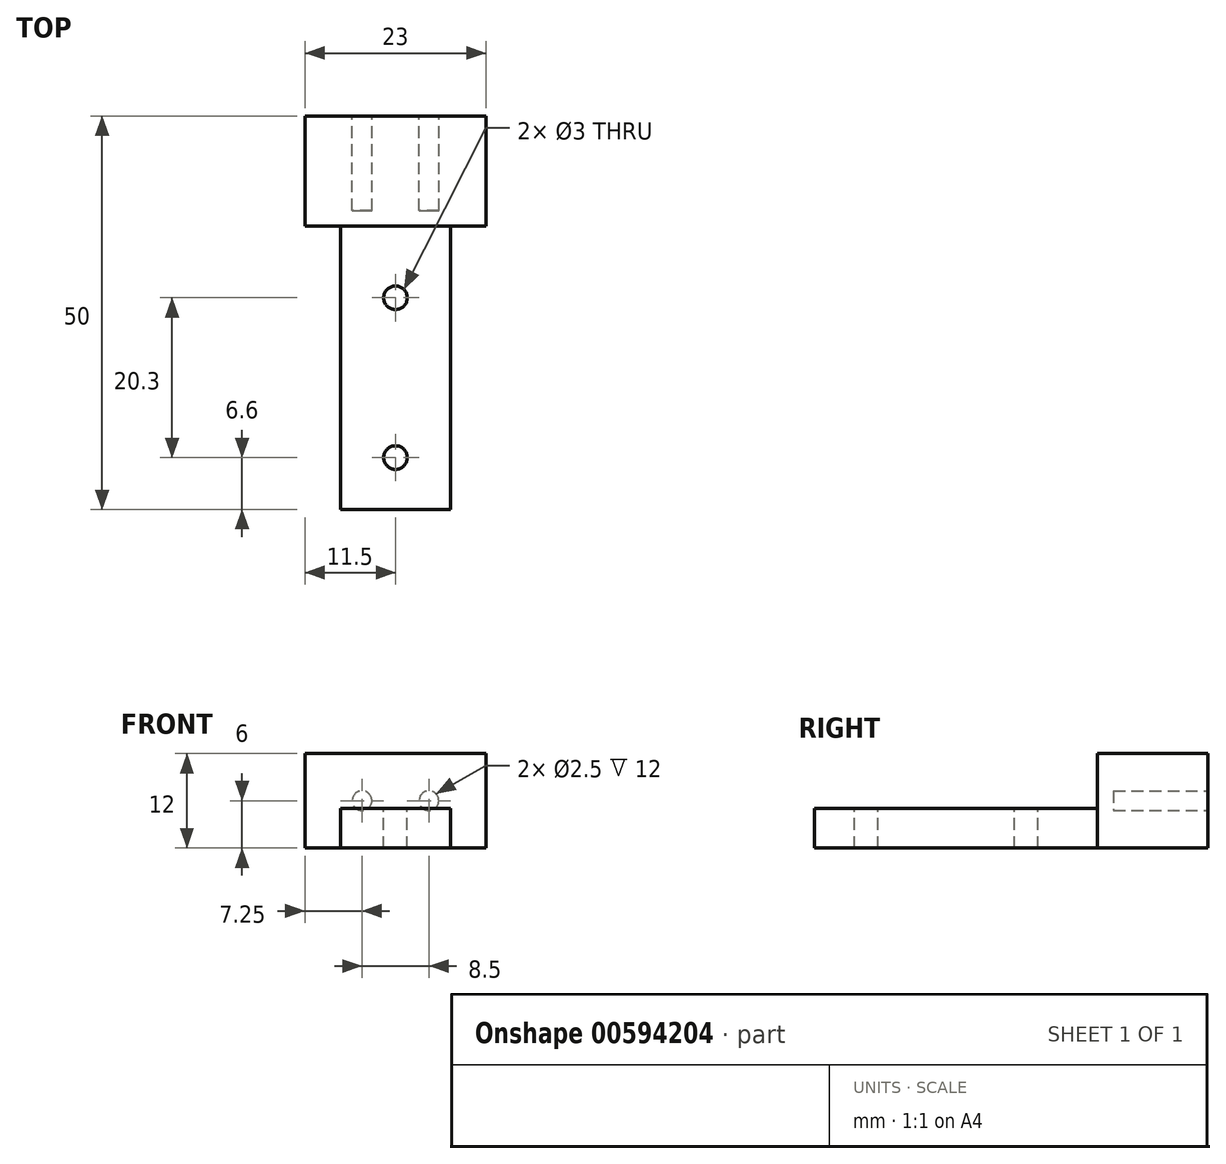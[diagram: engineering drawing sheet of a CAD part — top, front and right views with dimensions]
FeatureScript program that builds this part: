
annotation { "Feature Type Name" : "Feature", "Feature Type Description" : "" }
export const myFeature = defineFeature(function(context is Context, id is Id, definition is map)
    precondition{}
    {
        {
            var Q0;
            Q0=qCreatedBy(makeId("Top.planeOp"),FACE);
            var sketch = newSketch(context, id + "F0", { "sketchPlane" : qUnion([Q0])});
            skLineSegment(sketch, "E0.bottom", {"start": v(0, 0) * mm, "end": v(14, 0) * mm});
            skLineSegment(sketch, "E0.top", {"start": v(0, 58) * mm, "end": v(14, 58) * mm});
            skLineSegment(sketch, "E0.left", {"start": v(0, 0) * mm, "end": v(0, 58) * mm});
            skLineSegment(sketch, "E0.right", {"start": v(14, 0) * mm, "end": v(14, 58) * mm});
            skSolve(sketch);
        }
        {
            var Q0;
            Q0=makeQuery(id+"F0.imprint","IMPRINT",FACE,{"disambiguationData":[TD([[makeQuery(id+"F0.imprint","IMPRINT",EDGE,{"derivedFrom":sQuery(id+"F0.wireOp",EDGE,"E0.bottom")}),1.0]])]});
            extrude(context, id + "F1", {"entities" : qUnion([Q0]), "depth" : 5 * mm, "offsetDistance" : 25 * mm});
        }
        {
            var Q0;
            Q0=makeQuery(id+"F1.opExtrude","CAP_FACE",FACE,{"disambiguationData":[OSD([sQuery(id+"F0.wireOp",EDGE,"E0.bottom"),sQuery(id+"F0.wireOp",EDGE,"E0.top"),sQuery(id+"F0.wireOp",EDGE,"E0.left"),sQuery(id+"F0.wireOp",EDGE,"E0.right")])],"isStart":false});
            var sketch = newSketch(context, id + "F2", { "sketchPlane" : qUnion([Q0])});
            skLineSegment(sketch, "E1.bottom", {"start": v(0, 58) * mm, "end": v(14, 58) * mm});
            skLineSegment(sketch, "E1.top", {"start": v(0, 49.67) * mm, "end": v(14, 49.67) * mm});
            skLineSegment(sketch, "E1.left", {"start": v(0, 58) * mm, "end": v(0, 49.67) * mm});
            skLineSegment(sketch, "E1.right", {"start": v(14, 58) * mm, "end": v(14, 49.67) * mm});
            skLineSegment(sketch, "E2.bottom", {"start": v(0, 58) * mm, "end": v(1.75, 58) * mm});
            skLineSegment(sketch, "E2.top", {"start": v(0, 55.5) * mm, "end": v(1.75, 55.5) * mm});
            skLineSegment(sketch, "E2.left", {"start": v(0, 58) * mm, "end": v(0, 55.5) * mm});
            skLineSegment(sketch, "E2.right", {"start": v(1.75, 58) * mm, "end": v(1.75, 55.5) * mm});
            skLineSegment(sketch, "E3.bottom", {"start": v(14, 58) * mm, "end": v(12.25, 58) * mm});
            skLineSegment(sketch, "E3.top", {"start": v(14, 55.5) * mm, "end": v(12.25, 55.5) * mm});
            skLineSegment(sketch, "E3.left", {"start": v(14, 58) * mm, "end": v(14, 55.5) * mm});
            skLineSegment(sketch, "E3.right", {"start": v(12.25, 58) * mm, "end": v(12.25, 55.5) * mm});
            skCircle(sketch, "E4", {"center": v(1.75, 55.5) * mm, "radius": 1 * mm});
            skCircle(sketch, "E5", {"center": v(12.25, 55.5) * mm, "radius": 1 * mm});
            skLineSegment(sketch, "E6.bottom", {"start": v(1.75, 55.5) * mm, "end": v(7, 55.5) * mm});
            skLineSegment(sketch, "E6.top", {"start": v(1.75, 36.5) * mm, "end": v(7, 36.5) * mm});
            skLineSegment(sketch, "E6.left", {"start": v(1.75, 55.5) * mm, "end": v(1.75, 36.5) * mm});
            skLineSegment(sketch, "E6.right", {"start": v(7, 55.5) * mm, "end": v(7, 36.5) * mm});
            skLineSegment(sketch, "E7.top", {"start": v(1.75, 28.4) * mm, "end": v(7, 28.4) * mm});
            skLineSegment(sketch, "E7.left", {"start": v(1.75, 36.5) * mm, "end": v(1.75, 28.4) * mm});
            skLineSegment(sketch, "E7.right", {"start": v(7, 36.5) * mm, "end": v(7, 28.4) * mm});
            skLineSegment(sketch, "E8.top", {"start": v(1.75, 26.9) * mm, "end": v(7, 26.9) * mm});
            skLineSegment(sketch, "E8.left", {"start": v(1.75, 28.4) * mm, "end": v(1.75, 26.9) * mm});
            skLineSegment(sketch, "E8.right", {"start": v(7, 28.4) * mm, "end": v(7, 26.9) * mm});
            skCircle(sketch, "E9", {"center": v(7, 26.9) * mm, "radius": 1.5 * mm});
            skLineSegment(sketch, "E10.bottom", {"start": v(7, 26.9) * mm, "end": v(12.25, 26.9) * mm});
            skLineSegment(sketch, "E10.top", {"start": v(7, 6.6) * mm, "end": v(12.25, 6.6) * mm});
            skLineSegment(sketch, "E10.left", {"start": v(7, 26.9) * mm, "end": v(7, 6.6) * mm});
            skLineSegment(sketch, "E10.right", {"start": v(12.25, 26.9) * mm, "end": v(12.25, 6.6) * mm});
            skCircle(sketch, "E11", {"center": v(7, 6.6) * mm, "radius": 1.5 * mm});
            skSolve(sketch);
        }
        {
            var Q0;
            {var subQ0=sQuery(id+"F2.wireOp",EDGE,"E8.right");Q0=makeQuery(id+"F2.imprint","IMPRINT",FACE,{"disambiguationData":[TD([[makeQuery(id+"F2.imprint","IMPRINT",EDGE,{"derivedFrom":subQ0}),1.0]])]});}
            var Q1;
            {var subQ0=sQuery(id+"F2.wireOp",EDGE,"E8.right");Q1=makeQuery(id+"F2.imprint","IMPRINT",FACE,{"disambiguationData":[TD([[makeQuery(id+"F2.imprint","IMPRINT",EDGE,{"derivedFrom":subQ0}),-1.0]])]});}
            var Q2;
            {var subQ1=sQuery(id+"F2.wireOp",EDGE,"E8.top");var subQ3=sQuery(id+"F2.wireOp",EDGE,"E9");var subQ4=makeQuery(id+"F2.imprint","INTERSECT",VERTEX,{"derivedFrom":[subQ1,subQ3]});Q2=makeQuery(id+"F2.imprint","IMPRINT",FACE,{"disambiguationData":[TD([[makeQuery(id+"F2.imprint","IMPRINT",EDGE,{"disambiguationData":[TD([[subQ4,-1.0]])],"derivedFrom":subQ3}),1.0]])]});}
            var Q3;
            {var subQ0=sQuery(id+"F2.wireOp",EDGE,"E10.bottom");var subQ1=sQuery(id+"F2.wireOp",EDGE,"E9");var subQ2=makeQuery(id+"F2.imprint","INTERSECT",VERTEX,{"derivedFrom":[subQ1,subQ0]});Q3=makeQuery(id+"F2.imprint","IMPRINT",FACE,{"disambiguationData":[TD([[makeQuery(id+"F2.imprint","IMPRINT",EDGE,{"disambiguationData":[TD([[subQ2,1.0]])],"derivedFrom":subQ1}),1.0]])]});}
            var Q4;
            {var subQ0=sQuery(id+"F2.wireOp",EDGE,"E10.left");var subQ1=sQuery(id+"F2.wireOp",EDGE,"E10.top");var subQ2=makeQuery(id+"F2.imprint","INTERSECT",VERTEX,{"derivedFrom":[subQ1,subQ0]});Q4=makeQuery(id+"F2.imprint","IMPRINT",FACE,{"disambiguationData":[TD([[makeQuery(id+"F2.imprint","IMPRINT",EDGE,{"disambiguationData":[TD([[subQ2,-1.0]])],"derivedFrom":subQ1}),1.0]])]});}
            var Q5;
            {var subQ0=sQuery(id+"F2.wireOp",EDGE,"E10.left");var subQ1=sQuery(id+"F2.wireOp",EDGE,"E10.top");var subQ2=makeQuery(id+"F2.imprint","INTERSECT",VERTEX,{"derivedFrom":[subQ1,subQ0]});Q5=makeQuery(id+"F2.imprint","IMPRINT",FACE,{"disambiguationData":[TD([[makeQuery(id+"F2.imprint","IMPRINT",EDGE,{"disambiguationData":[TD([[subQ2,-1.0]])],"derivedFrom":subQ1}),-1.0]])]});}
            extrude(context, id + "F3", {"entities" : qUnion([Q0, Q1, Q2, Q3, Q4, Q5]), "operationType" : NewBodyOperationType.REMOVE, "oppositeDirection" : true, "depth" : 25 * mm, "offsetDistance" : 25 * mm});
        }
        {
            var Q0;
            Q0=makeQuery(id+"F1.opExtrude","SWEPT_FACE",FACE,{"disambiguationData":[OSD([sQuery(id+"F0.wireOp",EDGE,"E0.top")])]});
            cPlane(context, id + "F4", {"entities" : qUnion([Q0]), "cplaneType" : CPlaneType.OFFSET, "offset" : 2.5 * mm, "oppositeDirection" : true, "width" : 150 * mm, "height" : 150 * mm});
        }
        {
            var Q0;
            Q0=qCreatedBy(id+"F4.planeOp",FACE);
            var sketch = newSketch(context, id + "F5", { "sketchPlane" : qUnion([Q0])});
            skLineSegment(sketch, "E12.bottom", {"start": v(0, 0) * mm, "end": v(4.5, 0) * mm});
            skLineSegment(sketch, "E12.top", {"start": v(0, -3.5) * mm, "end": v(4.5, -3.5) * mm});
            skLineSegment(sketch, "E12.left", {"start": v(0, 0) * mm, "end": v(0, -3.5) * mm});
            skLineSegment(sketch, "E12.right", {"start": v(4.5, 0) * mm, "end": v(4.5, -3.5) * mm});
            skLineSegment(sketch, "E13.bottom", {"start": v(4.5, -3.5) * mm, "end": v(-18.5, -3.5) * mm});
            skLineSegment(sketch, "E13.top", {"start": v(4.5, 8.5) * mm, "end": v(-18.5, 8.5) * mm});
            skLineSegment(sketch, "E13.left", {"start": v(4.5, -3.5) * mm, "end": v(4.5, 8.5) * mm});
            skLineSegment(sketch, "E13.right", {"start": v(-18.5, -3.5) * mm, "end": v(-18.5, 8.5) * mm});
            skLineSegment(sketch, "E14.bottom", {"start": v(4.5, 0) * mm, "end": v(-18.5, 0) * mm});
            skLineSegment(sketch, "E14.top", {"start": v(4.5, 12) * mm, "end": v(-18.5, 12) * mm});
            skLineSegment(sketch, "E14.left", {"start": v(4.5, 0) * mm, "end": v(4.5, 12) * mm});
            skLineSegment(sketch, "E14.right", {"start": v(-18.5, 0) * mm, "end": v(-18.5, 12) * mm});
            skSolve(sketch);
        }
        {
            var Q0;
            {var subQ0=sQuery(id+"F5.wireOp",EDGE,"E13.top");Q0=makeQuery(id+"F5.imprint","IMPRINT",FACE,{"disambiguationData":[TD([[makeQuery(id+"F5.imprint","IMPRINT",EDGE,{"derivedFrom":subQ0}),-1.0]])]});}
            var Q1;
            {var subQ1=sQuery(id+"F5.wireOp",EDGE,"E13.top");Q1=makeQuery(id+"F5.imprint","IMPRINT",FACE,{"disambiguationData":[TD([[makeQuery(id+"F5.imprint","IMPRINT",EDGE,{"derivedFrom":subQ1}),1.0]])]});}
            extrude(context, id + "F6", {"entities" : qUnion([Q0, Q1]), "operationType" : NewBodyOperationType.ADD, "oppositeDirection" : true, "depth" : 19.5 * mm, "offsetDistance" : 25 * mm});
        }
        {
            var Q0;
            Q0=makeQuery(id+"F1.opExtrude","SWEPT_FACE",FACE,{"disambiguationData":[OSD([sQuery(id+"F0.wireOp",EDGE,"E0.top")])]});
            var sketch = newSketch(context, id + "F7", { "sketchPlane" : qUnion([Q0])});
            skLineSegment(sketch, "E15.bottom", {"start": v(0, 0) * mm, "end": v(-18.5, 0) * mm});
            skLineSegment(sketch, "E15.top", {"start": v(0, 8.5) * mm, "end": v(-18.5, 8.5) * mm});
            skLineSegment(sketch, "E15.left", {"start": v(0, 0) * mm, "end": v(0, 8.5) * mm});
            skLineSegment(sketch, "E15.right", {"start": v(-18.5, 0) * mm, "end": v(-18.5, 8.5) * mm});
            skLineSegment(sketch, "E16.bottom", {"start": v(0, 0) * mm, "end": v(4.5, 0) * mm});
            skLineSegment(sketch, "E16.top", {"start": v(0, -3.5) * mm, "end": v(4.5, -3.5) * mm});
            skLineSegment(sketch, "E16.left", {"start": v(0, 0) * mm, "end": v(0, -3.5) * mm});
            skLineSegment(sketch, "E16.right", {"start": v(4.5, 0) * mm, "end": v(4.5, -3.5) * mm});
            skLineSegment(sketch, "E17.bottom", {"start": v(4.5, -3.5) * mm, "end": v(-18.5, -3.5) * mm});
            skLineSegment(sketch, "E17.top", {"start": v(4.5, 8.5) * mm, "end": v(-18.5, 8.5) * mm});
            skLineSegment(sketch, "E17.left", {"start": v(4.5, -3.5) * mm, "end": v(4.5, 8.5) * mm});
            skLineSegment(sketch, "E17.right", {"start": v(-18.5, -3.5) * mm, "end": v(-18.5, 8.5) * mm});
            skLineSegment(sketch, "E18.bottom", {"start": v(4.5, 0) * mm, "end": v(-18.5, 0) * mm});
            skLineSegment(sketch, "E18.top", {"start": v(4.5, 12) * mm, "end": v(-18.5, 12) * mm});
            skLineSegment(sketch, "E18.left", {"start": v(4.5, 0) * mm, "end": v(4.5, 12) * mm});
            skLineSegment(sketch, "E18.right", {"start": v(-18.5, 0) * mm, "end": v(-18.5, 12) * mm});
            skSolve(sketch);
        }
        {
            var Q0;
            {var subQ3=sQuery(id+"F0.wireOp",EDGE,"E0.top");var subQ4=makeQuery(id+"F1.opExtrude","CAP_EDGE",EDGE,{"disambiguationData":[OSD([subQ3])],"isStart":false});Q0=makeQuery(id+"F7.imprint","IMPRINT",FACE,{"disambiguationData":[TD([[makeQuery(id+"F7.imprint","IMPRINT",EDGE,{"derivedFrom":subQ4}),1.0]])]});}
            var Q1;
            {var subQ5=sQuery(id+"F0.wireOp",EDGE,"E0.top");var subQ9=makeQuery(id+"F1.opExtrude","CAP_EDGE",EDGE,{"disambiguationData":[OSD([subQ5])],"isStart":false});Q1=makeQuery(id+"F7.imprint","IMPRINT",FACE,{"disambiguationData":[TD([[makeQuery(id+"F7.imprint","IMPRINT",EDGE,{"derivedFrom":subQ9}),-1.0]])]});}
            var Q2;
            {var subQ1=sQuery(id+"F7.wireOp",EDGE,"E15.left");var subQ6=sQuery(id+"F7.wireOp",EDGE,"E17.top");var subQ7=makeQuery(id+"F7.imprint","INTERSECT",VERTEX,{"derivedFrom":[subQ1,subQ6]});Q2=makeQuery(id+"F7.imprint","IMPRINT",FACE,{"disambiguationData":[TD([[makeQuery(id+"F7.imprint","IMPRINT",EDGE,{"disambiguationData":[TD([[subQ7,1.0]])],"derivedFrom":subQ1}),-1.0]])]});}
            var Q3;
            {var subQ3=sQuery(id+"F7.wireOp",EDGE,"E18.top");Q3=makeQuery(id+"F7.imprint","IMPRINT",FACE,{"disambiguationData":[TD([[makeQuery(id+"F7.imprint","IMPRINT",EDGE,{"derivedFrom":subQ3}),1.0]])]});}
            extrude(context, id + "F8", {"entities" : qUnion([Q0, Q1, Q2, Q3]), "operationType" : NewBodyOperationType.REMOVE, "oppositeDirection" : true, "depth" : 8 * mm, "offsetDistance" : 25 * mm});
        }
        {
            var Q0;
            Q0=makeQuery(id+"F8.boolean.opBoolean","COPY",FACE,{"derivedFrom":makeQuery(id+"F8.opExtrude","CAP_FACE",FACE,{"disambiguationData":[OSD([sQuery(id+"F7.wireOp",EDGE,"E18.bottom"),sQuery(id+"F7.wireOp",EDGE,"E18.top"),sQuery(id+"F7.wireOp",EDGE,"E18.left"),sQuery(id+"F7.wireOp",EDGE,"E18.right")])],"isStart":false})});
            var sketch = newSketch(context, id + "F9", { "sketchPlane" : qUnion([Q0])});
            skLineSegment(sketch, "E19.bottom", {"start": v(-18.5, 12) * mm, "end": v(-11.25, 12) * mm});
            skLineSegment(sketch, "E19.top", {"start": v(-18.5, 6) * mm, "end": v(-11.25, 6) * mm});
            skLineSegment(sketch, "E19.left", {"start": v(-18.5, 12) * mm, "end": v(-18.5, 6) * mm});
            skLineSegment(sketch, "E19.right", {"start": v(-11.25, 12) * mm, "end": v(-11.25, 6) * mm});
            skLineSegment(sketch, "E20.bottom", {"start": v(4.5, 12) * mm, "end": v(-2.75, 12) * mm});
            skLineSegment(sketch, "E20.top", {"start": v(4.5, 6) * mm, "end": v(-2.75, 6) * mm});
            skLineSegment(sketch, "E20.left", {"start": v(4.5, 12) * mm, "end": v(4.5, 6) * mm});
            skLineSegment(sketch, "E20.right", {"start": v(-2.75, 12) * mm, "end": v(-2.75, 6) * mm});
            skCircle(sketch, "E21", {"center": v(-11.25, 6) * mm, "radius": 1.25 * mm});
            skCircle(sketch, "E22", {"center": v(-2.75, 6) * mm, "radius": 1.25 * mm});
            skSolve(sketch);
        }
        {
            var Q0;
            {var subQ0=sQuery(id+"F9.wireOp",EDGE,"E19.right");var subQ1=sQuery(id+"F9.wireOp",EDGE,"E19.top");var subQ2=makeQuery(id+"F9.imprint","INTERSECT",VERTEX,{"derivedFrom":[subQ1,subQ0]});Q0=makeQuery(id+"F9.imprint","IMPRINT",FACE,{"disambiguationData":[TD([[makeQuery(id+"F9.imprint","IMPRINT",EDGE,{"disambiguationData":[TD([[subQ2,1.0]])],"derivedFrom":subQ1}),-1.0]])]});}
            var Q1;
            {var subQ0=sQuery(id+"F9.wireOp",EDGE,"E19.right");var subQ1=sQuery(id+"F9.wireOp",EDGE,"E19.top");var subQ2=makeQuery(id+"F9.imprint","INTERSECT",VERTEX,{"derivedFrom":[subQ1,subQ0]});Q1=makeQuery(id+"F9.imprint","IMPRINT",FACE,{"disambiguationData":[TD([[makeQuery(id+"F9.imprint","IMPRINT",EDGE,{"disambiguationData":[TD([[subQ2,1.0]])],"derivedFrom":subQ1}),1.0]])]});}
            var Q2;
            {var subQ0=sQuery(id+"F9.wireOp",EDGE,"E20.right");var subQ1=sQuery(id+"F9.wireOp",EDGE,"E20.top");var subQ2=makeQuery(id+"F9.imprint","INTERSECT",VERTEX,{"derivedFrom":[subQ1,subQ0]});Q2=makeQuery(id+"F9.imprint","IMPRINT",FACE,{"disambiguationData":[TD([[makeQuery(id+"F9.imprint","IMPRINT",EDGE,{"disambiguationData":[TD([[subQ2,1.0]])],"derivedFrom":subQ1}),-1.0]])]});}
            var Q3;
            {var subQ0=sQuery(id+"F9.wireOp",EDGE,"E20.right");var subQ1=sQuery(id+"F9.wireOp",EDGE,"E20.top");var subQ2=makeQuery(id+"F9.imprint","INTERSECT",VERTEX,{"derivedFrom":[subQ1,subQ0]});Q3=makeQuery(id+"F9.imprint","IMPRINT",FACE,{"disambiguationData":[TD([[makeQuery(id+"F9.imprint","IMPRINT",EDGE,{"disambiguationData":[TD([[subQ2,1.0]])],"derivedFrom":subQ1}),1.0]])]});}
            extrude(context, id + "F10", {"entities" : qUnion([Q0, Q1, Q2, Q3]), "operationType" : NewBodyOperationType.REMOVE, "oppositeDirection" : true, "depth" : 12 * mm, "offsetDistance" : 25 * mm});
        }
    });
